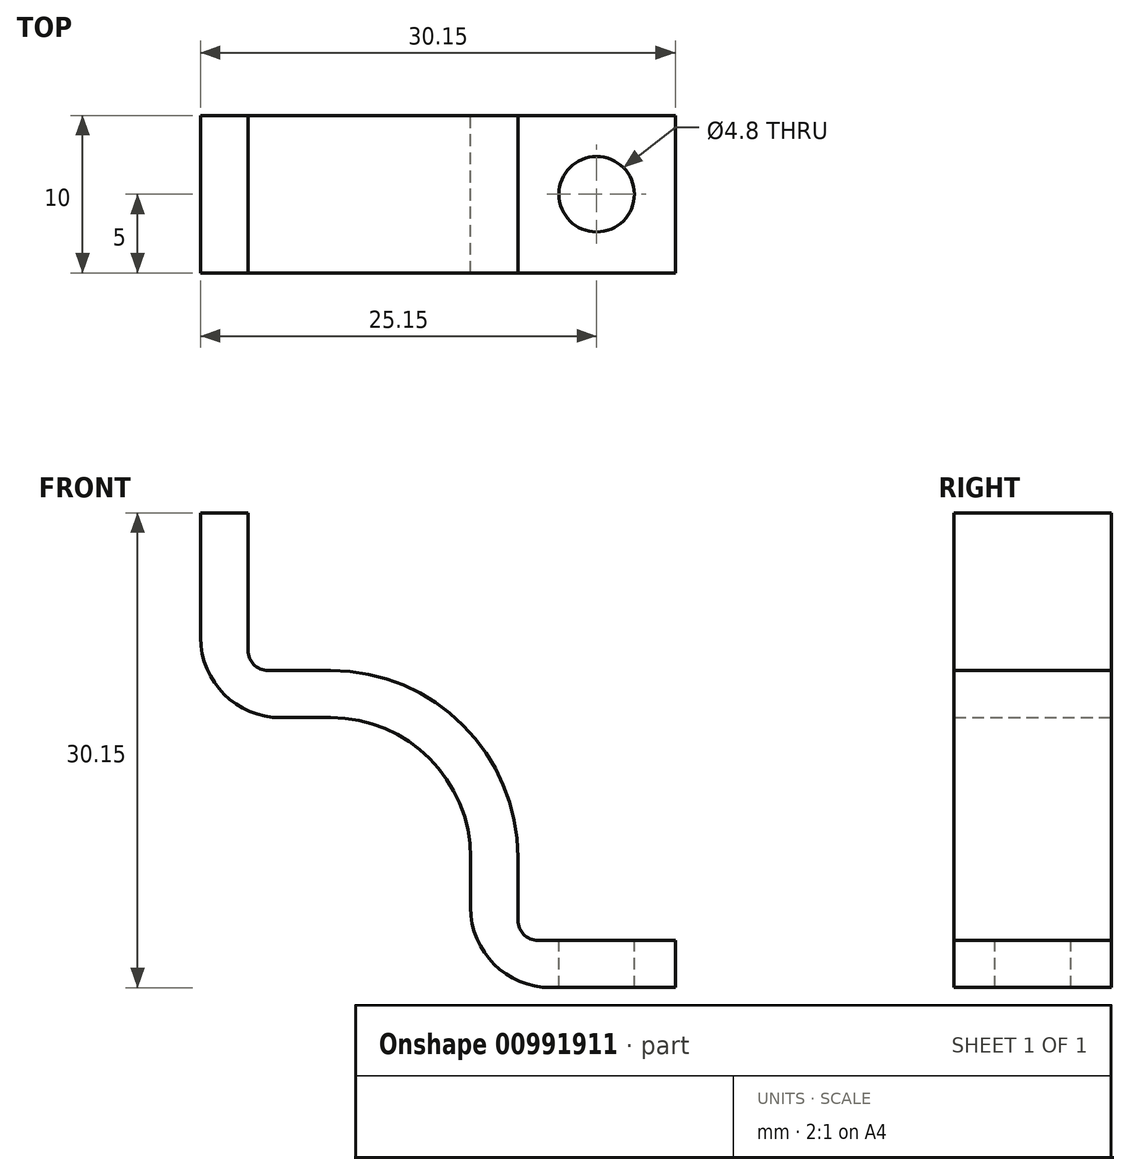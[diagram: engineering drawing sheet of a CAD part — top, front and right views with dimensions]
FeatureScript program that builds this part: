
annotation { "Feature Type Name" : "Feature", "Feature Type Description" : "" }
export const myFeature = defineFeature(function(context is Context, id is Id, definition is map)
    precondition{}
    {
        {
            var Q0;
            Q0=qCreatedBy(makeId("Front.planeOp"),FACE);
            var sketch = newSketch(context, id + "F0", { "sketchPlane" : qUnion([Q0])});
            skArc(sketch, "E0", {"start": v(8.9, 0) * mm, "mid": v(6.29, 6.29) * mm, "end": v(0, 8.9) * mm});
            skLineSegment(sketch, "E1", {"start": v(0, 0) * mm, "end": v(6.29, 6.29) * mm, "construction": true});
            skLineSegment(sketch, "E2", {"start": v(8.89, 0) * mm, "end": v(8.89, -8.26) * mm});
            skLineSegment(sketch, "E3", {"start": v(8.9, -8.26) * mm, "end": v(21.9, -8.25) * mm});
            skLineSegment(sketch, "E4", {"start": v(21.9, -8.25) * mm, "end": v(21.9, -5.25) * mm});
            skLineSegment(sketch, "E5", {"start": v(21.9, -5.25) * mm, "end": v(11.9, -5.25) * mm});
            skLineSegment(sketch, "E6", {"start": v(11.89, -5.25) * mm, "end": v(11.89, 0) * mm});
            skArc(sketch, "E7", {"start": v(11.89, 0) * mm, "mid": v(8.4, 8.4) * mm, "end": v(0, 11.89) * mm});
            skLineSegment(sketch, "E8.MirrorCS", {"start": v(-8.26, 21.9) * mm, "end": v(-5.26, 21.9) * mm});
            skLineSegment(sketch, "E9.MirrorCS", {"start": v(-8.25, 8.89) * mm, "end": v(-8.26, 21.89) * mm});
            skLineSegment(sketch, "E10.MirrorCS", {"start": v(-5.26, 21.89) * mm, "end": v(-5.25, 11.89) * mm});
            skLineSegment(sketch, "E11.MirrorCS", {"start": v(0, 8.89) * mm, "end": v(-8.26, 8.89) * mm});
            skLineSegment(sketch, "E12.MirrorCS", {"start": v(-5.26, 11.89) * mm, "end": v(0, 11.89) * mm});
            skSolve(sketch);
        }
        {
            var Q0;
            Q0=makeQuery(id+"F0.imprint","IMPRINT",FACE,{"disambiguationData":[TD([[makeQuery(id+"F0.imprint","IMPRINT",EDGE,{"derivedFrom":sQuery(id+"F0.wireOp",EDGE,"E0")}),-1.0]])]});
            extrude(context, id + "F1", {"entities" : qUnion([Q0]), "depth" : 10 * mm});
        }
        {
            var Q0;
            Q0=makeQuery(id+"F1.opExtrude","SWEPT_FACE",FACE,{"disambiguationData":[OSD([sQuery(id+"F0.wireOp",EDGE,"E5")])]});
            var sketch = newSketch(context, id + "F2", { "sketchPlane" : qUnion([Q0])});
            skCircle(sketch, "E13", {"center": v(16.9, -5) * mm, "radius": 2.4 * mm});
            skSolve(sketch);
        }
        {
            var Q0;
            Q0=qSketchRegion(id+"F2",true);
            extrude(context, id + "F3", {"entities" : qUnion([Q0]), "operationType" : NewBodyOperationType.REMOVE, "endBound" : BoundingType.UP_TO_NEXT, "oppositeDirection" : true, "depth" : 25.4 * mm});
        }
        {
            var Q0;
            Q0=makeQuery(id+"F1.opExtrude","CAP_EDGE",EDGE,{"disambiguationData":[OSD([sQuery(id+"F0.wireOp",EDGE,"E0")])],"isStart":true});
            cPoint(context, id + "F4", {"entities" : qUnion([Q0]), "parameter" : 0.5});
        }
        {
            var Q0;
            Q0=makeQuery(id+"F1.opExtrude","CAP_EDGE",EDGE,{"disambiguationData":[OSD([sQuery(id+"F0.wireOp",EDGE,"E0")])],"isStart":false});
            cPoint(context, id + "F5", {"entities" : qUnion([Q0]), "parameter" : 0.5});
        }
        {
            var Q0;
            Q0=qCreatedBy(makeId("Origin.pointOp"),VERTEX);
            var Q1;
            Q1=qCreatedBy(id+"F4",VERTEX);
            var Q2;
            Q2=qCreatedBy(id+"F5",VERTEX);
            cPlane(context, id + "F6", {"entities" : qUnion([Q0, Q1, Q2]), "cplaneType" : CPlaneType.THREE_POINT, "offset" : 25.4 * mm, "width" : 152.4 * mm, "height" : 152.4 * mm});
        }
        {
            var Q0;
            Q0=makeQuery(id+"F1.opExtrude","SWEPT_EDGE",EDGE,{"disambiguationData":[OSD([sQuery(id+"F0.wireOp",EDGE,"E9.MirrorCS"),sQuery(id+"F0.wireOp",EDGE,"E11.MirrorCS")])]});
            var Q1;
            Q1=makeQuery(id+"F1.opExtrude","SWEPT_EDGE",EDGE,{"disambiguationData":[OSD([sQuery(id+"F0.wireOp",EDGE,"E2"),sQuery(id+"F0.wireOp",EDGE,"E3")])]});
            fillet(context, id + "F7", {"entities" : qUnion([Q0, Q1]), "radius" : 5.08 * mm, "tangentPropagation" : true, "allowEdgeOverflow" : false});
        }
        {
            var Q0;
            Q0=makeQuery(id+"F1.opExtrude","SWEPT_EDGE",EDGE,{"disambiguationData":[OSD([sQuery(id+"F0.wireOp",EDGE,"E10.MirrorCS"),sQuery(id+"F0.wireOp",EDGE,"E12.MirrorCS")])]});
            var Q1;
            Q1=makeQuery(id+"F1.opExtrude","SWEPT_EDGE",EDGE,{"disambiguationData":[OSD([sQuery(id+"F0.wireOp",EDGE,"E5"),sQuery(id+"F0.wireOp",EDGE,"E6")])]});
            fillet(context, id + "F8", {"entities" : qUnion([Q0, Q1]), "radius" : 1.27 * mm, "tangentPropagation" : true, "allowEdgeOverflow" : false});
        }
    });
